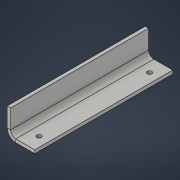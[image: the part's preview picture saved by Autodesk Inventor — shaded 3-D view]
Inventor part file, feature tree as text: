
AUTODESK INVENTOR PART (.ipt)
format: ipt  version: 2022.2 (Build 262287000, 287)  size: 135,680 bytes
history: native  units: in
note: dims shown in document units (in); Inventor stores cm internally (conversion verified against a paired STEP export)
features: sheet_metal_op x4, sketch x3, other x2, hole x1
ambient origin geometry x8: Origin, YZ Plane, XZ Plane, XY Plane, X Axis, Y Axis, Z Axis, Center Point
bodies: Solid1 (feature_tree)
feature tree (10):
  sheet_metal_op  "Face1"
  sheet_metal_op  "Flange1"
  hole  "Hole1"  [1 undecoded]
  sketch  "Sketch1"  dims[d0=1.0in d1=5.0in]
  other  "Plate1"
  sketch  "Sketch2"  dims[d2=0.125in]
  other  "Plate2"
  sheet_metal_op  "Bend1"
  sheet_metal_op  "Corner1"
  sketch  "Sketch3"  dims[d3=0.125in d4=0.0625in d5=0.25in d6=0.1875in d7=1.0in d8=90.0deg d9=0.1875in d10=0.5in d11=0.125in d12=0.1875in d13=0.5in d14=0.5in d15=0.161in d16=0.75in d17=0.375in d18=0.06in d19=0.5635in d20=0.125in d21=0.8108in]
note: 1 required parameter value undecoded (feature->parameter linkage not recoverable at this tier; creation-order binding heuristic only, values carry confidence <= 0.55)
